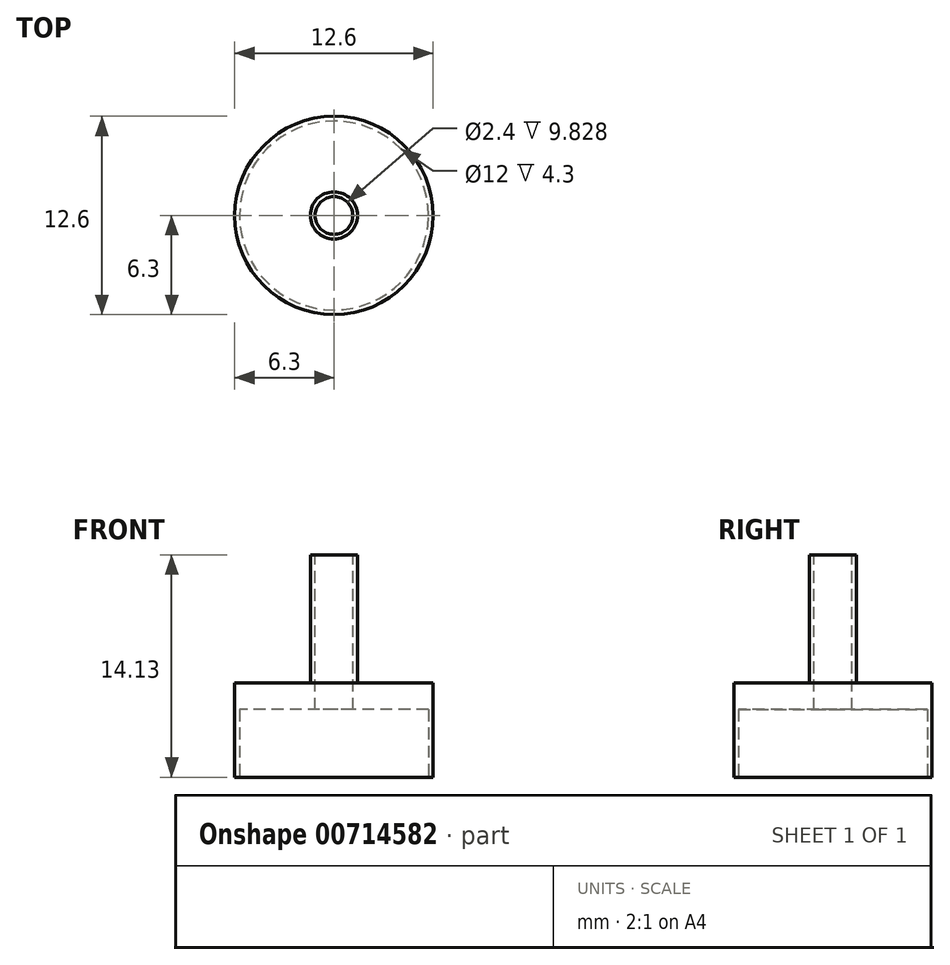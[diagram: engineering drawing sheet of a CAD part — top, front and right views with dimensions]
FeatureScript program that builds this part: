
annotation { "Feature Type Name" : "Feature", "Feature Type Description" : "" }
export const myFeature = defineFeature(function(context is Context, id is Id, definition is map)
    precondition{}
    {
        {
            var Q0;
            Q0=qCreatedBy(makeId("Top.planeOp"),FACE);
            var sketch = newSketch(context, id + "F0", { "sketchPlane" : qUnion([Q0])});
            skCircle(sketch, "E0", {"center": v(0, 0) * mm, "radius": 6 * mm});
            skCircle(sketch, "E1", {"center": v(0, 0) * mm, "radius": 6.3 * mm});
            skSolve(sketch);
        }
        {
            var Q0;
            Q0=qCreatedBy(makeId("Top.planeOp"),FACE);
            cPlane(context, id + "F1", {"entities" : qUnion([Q0]), "cplaneType" : CPlaneType.OFFSET, "offset" : 8 * mm, "width" : 152.4 * mm, "height" : 152.4 * mm});
        }
        {
            var Q0;
            Q0 = qSketchRegion(id + "F0", true);
            var Q1;
            Q1=makeQuery(id+"F0.imprint","IMPRINT",FACE,{"disambiguationData":[TD([[makeQuery(id+"F0.imprint","IMPRINT",EDGE,{"derivedFrom":sQuery(id+"F0.wireOp",EDGE,"E0")}),1.0]])]});
            extrude(context, id + "F2", {"entities" : qUnion([Q0, Q1]), "depth" : 6 * mm, "offsetDistance" : 25.4 * mm});
        }
        {
            var Q0;
            Q0=makeQuery(id+"F2.opExtrude","CAP_FACE",FACE,{"disambiguationData":[OSD([sQuery(id+"F0.wireOp",EDGE,"E1")])],"isStart":false});
            var sketch = newSketch(context, id + "F3", { "sketchPlane" : qUnion([Q0])});
            skCircle(sketch, "E2", {"center": v(0, 0) * mm, "radius": 1.5 * mm});
            skSolve(sketch);
        }
        {
            var Q0;
            Q0 = qSketchRegion(id + "F3", true);
            extrude(context, id + "F4", {"entities" : qUnion([Q0]), "operationType" : NewBodyOperationType.ADD, "depth" : 8.13 * mm, "offsetDistance" : 25.4 * mm});
        }
        {
            var Q0;
            Q0=makeQuery(id+"F4.opExtrude","CAP_FACE",FACE,{"disambiguationData":[OSD([sQuery(id+"F3.wireOp",EDGE,"E2")])],"isStart":false});
            var sketch = newSketch(context, id + "F5", { "sketchPlane" : qUnion([Q0])});
            skCircle(sketch, "E3", {"center": v(0, 0) * mm, "radius": 1.2 * mm});
            skSolve(sketch);
        }
        {
            var Q0;
            Q0 = qSketchRegion(id + "F5", true);
            extrude(context, id + "F6", {"entities" : qUnion([Q0]), "operationType" : NewBodyOperationType.REMOVE, "oppositeDirection" : true, "depth" : 25.4 * mm, "offsetDistance" : 25.4 * mm});
        }
        {
            var Q0;
            Q0=makeQuery(id+"F0.imprint","IMPRINT",FACE,{"disambiguationData":[TD([[makeQuery(id+"F0.imprint","IMPRINT",EDGE,{"derivedFrom":sQuery(id+"F0.wireOp",EDGE,"E0")}),1.0]])]});
            extrude(context, id + "F7", {"entities" : qUnion([Q0]), "operationType" : NewBodyOperationType.REMOVE, "depth" : 4.3 * mm, "offsetDistance" : 25.4 * mm});
        }
    });
